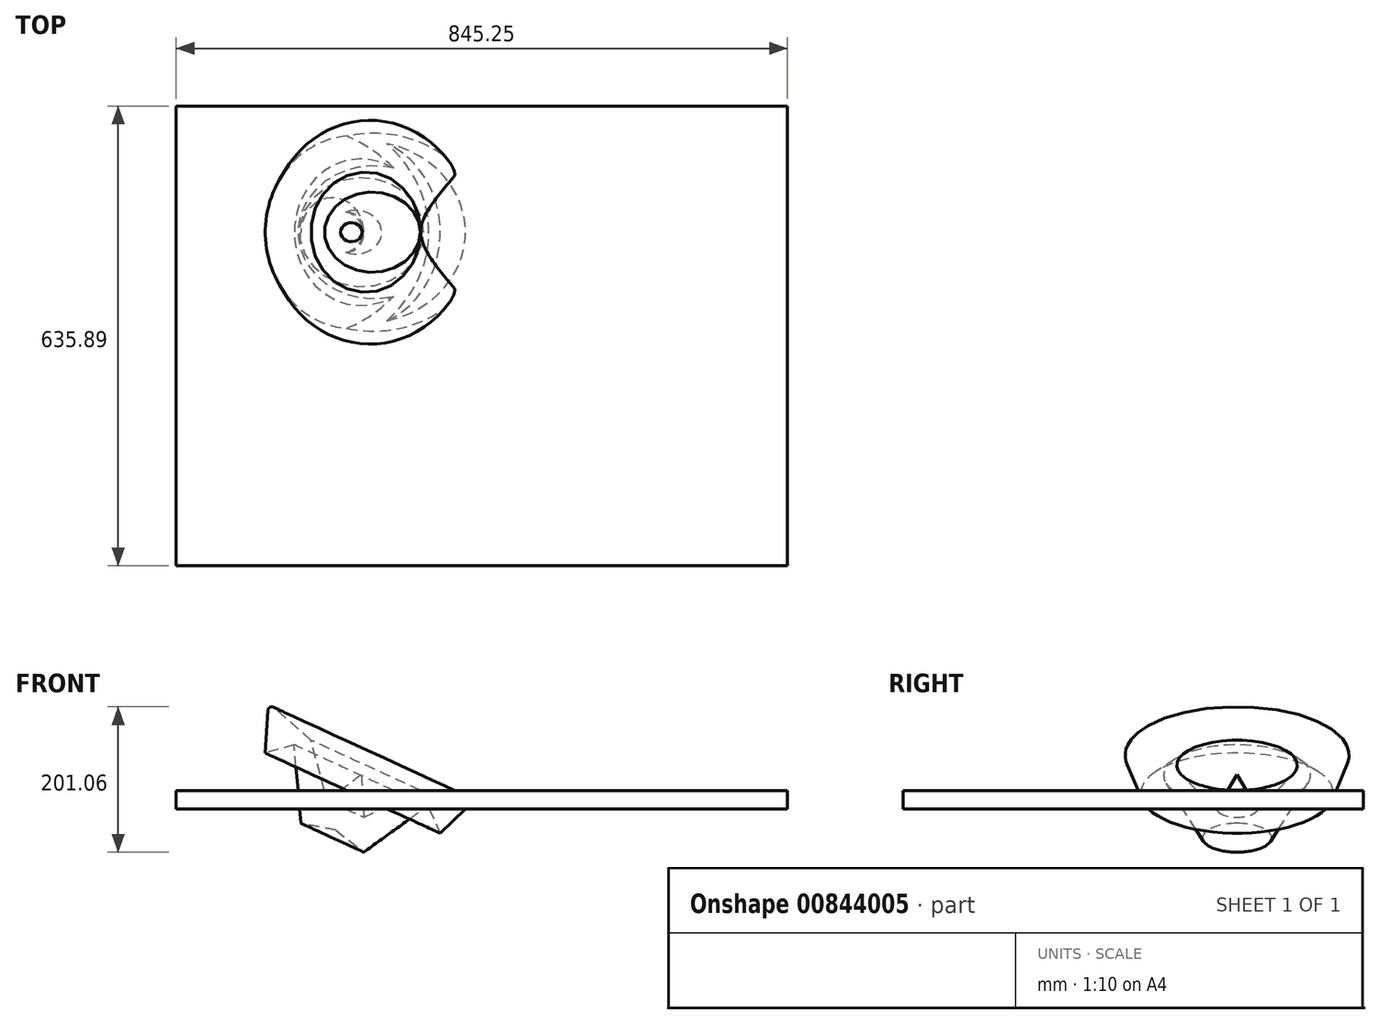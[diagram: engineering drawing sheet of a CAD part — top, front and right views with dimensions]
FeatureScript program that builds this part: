
annotation { "Feature Type Name" : "Feature", "Feature Type Description" : "" }
export const myFeature = defineFeature(function(context is Context, id is Id, definition is map)
    precondition{}
    {
        {
            var Q0;
            Q0=qCreatedBy(makeId("Front.planeOp"),FACE);
            var sketch = newSketch(context, id + "F0", { "sketchPlane" : qUnion([Q0])});
            skLineSegment(sketch, "E0", {"start": v(-34.4, 47.06) * mm, "end": v(-69.5, -29.5) * mm});
            skLineSegment(sketch, "E1", {"start": v(-69.5, -29.5) * mm, "end": v(-30.94, -60) * mm});
            skLineSegment(sketch, "E2", {"start": v(-30.94, -60) * mm, "end": v(57.42, 3.89) * mm});
            skLineSegment(sketch, "E3", {"start": v(57.42, 3.89) * mm, "end": v(74.97, -33.82) * mm});
            skLineSegment(sketch, "E4", {"start": v(74.97, -33.82) * mm, "end": v(124.76, 14.82) * mm});
            skLineSegment(sketch, "E5", {"start": v(124.76, 14.82) * mm, "end": v(47.34, 25.47) * mm});
            skLineSegment(sketch, "E6", {"start": v(47.34, 25.47) * mm, "end": v(-30.65, -11.66) * mm});
            skLineSegment(sketch, "E7", {"start": v(-30.65, -11.66) * mm, "end": v(-34.4, 47.06) * mm});
            skSolve(sketch);
        }
        {
            var Q0;
            Q0 = qSketchRegion(id + "F0", true);
            var Q1;
            Q1=sQuery(id+"F0.wireOp",EDGE,"E0");
            revolve(context, id + "F1", {"surfaceOperationType" : NewSurfaceOperationType.NEW, "entities" : qUnion([Q0]), "axis" : qUnion([Q1]), "revolveType" : RevolveType.FULL});
        }
        {
            var Q0;
            Q0=makeQuery(id+"F1.opRevolve","SWEPT_EDGE",EDGE,{"disambiguationData":[OSD([sQuery(id+"F0.wireOp",EDGE,"E4"),sQuery(id+"F0.wireOp",EDGE,"E5")])]});
            fillet(context, id + "F2", {"entities" : qUnion([Q0]), "radius" : 5.08 * mm, "tangentPropagation" : true, "allowEdgeOverflow" : false});
        }
        {
            var Q0;
            Q0=qCreatedBy(makeId("Top.planeOp"),FACE);
            var sketch = newSketch(context, id + "F3", { "sketchPlane" : qUnion([Q0])});
            skLineSegment(sketch, "E8.bottom", {"start": v(-290.28, 174.38) * mm, "end": v(554.97, 174.38) * mm});
            skLineSegment(sketch, "E8.top", {"start": v(-290.28, -461.5) * mm, "end": v(554.97, -461.5) * mm});
            skLineSegment(sketch, "E8.left", {"start": v(-290.28, 174.38) * mm, "end": v(-290.28, -461.5) * mm});
            skLineSegment(sketch, "E8.right", {"start": v(554.97, 174.38) * mm, "end": v(554.97, -461.5) * mm});
            skPoint(sketch, "E8.middle", {"position": v(132.35, -143.57) * mm});
            skSolve(sketch);
        }
        {
            var Q0;
            Q0 = qSketchRegion(id + "F3", true);
            extrude(context, id + "F4", {"entities" : qUnion([Q0]), "operationType" : NewBodyOperationType.ADD, "depth" : 25.4 * mm, "offsetDistance" : 25.4 * mm});
        }
    });
